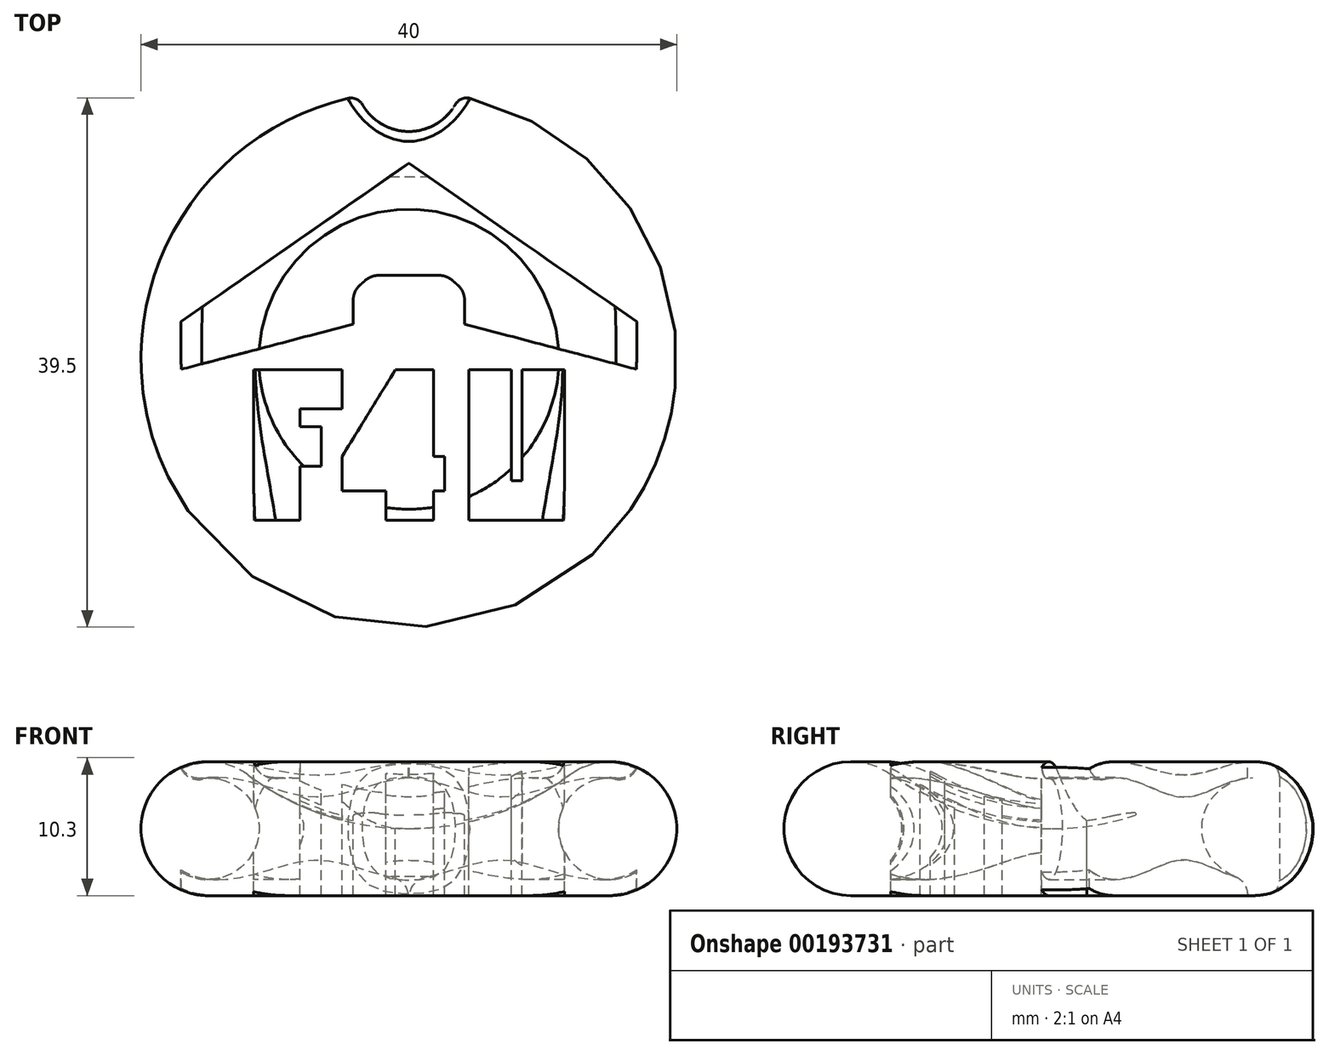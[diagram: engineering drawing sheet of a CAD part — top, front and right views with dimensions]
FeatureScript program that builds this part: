
annotation { "Feature Type Name" : "Feature", "Feature Type Description" : "" }
export const myFeature = defineFeature(function(context is Context, id is Id, definition is map)
    precondition{}
    {
        {
            var Q0;
            Q0=qCreatedBy(makeId("Front.planeOp"),FACE);
            var sketch = newSketch(context, id + "F0", { "sketchPlane" : qUnion([Q0])});
            skArc(sketch, "E0", {"start": v(-12, 9) * mm, "mid": v(-19.74, 6.58) * mm, "end": v(-15, 0) * mm});
            skArc(sketch, "E1", {"start": v(-12, 9) * mm, "mid": v(-6.32, 6.03) * mm, "end": v(0, 5) * mm});
            skLineSegment(sketch, "E2", {"start": v(-15, 0) * mm, "end": v(0, 0) * mm});
            skLineSegment(sketch, "E3", {"start": v(0, 0) * mm, "end": v(0, 5) * mm});
            skSolve(sketch);
        }
        {
            var Q0;
            Q0=makeQuery(id+"F0.imprint","IMPRINT",FACE,{"disambiguationData":[TD([[makeQuery(id+"F0.imprint","IMPRINT",EDGE,{"derivedFrom":sQuery(id+"F0.wireOp",EDGE,"E0")}),1.0]])]});
            var Q1;
            Q1=sQuery(id+"F0.wireOp",EDGE,"E3");
            revolve(context, id + "F1", {"entities" : qUnion([Q0]), "axis" : qUnion([Q1]), "revolveType" : RevolveType.FULL});
        }
        {
            var Q0;
            Q0=qCreatedBy(makeId("Top.planeOp"),FACE);
            cPlane(context, id + "F2", {"entities" : qUnion([Q0]), "cplaneType" : CPlaneType.OFFSET, "offset" : 10 * mm, "width" : 150 * mm, "height" : 150 * mm});
        }
        {
            var Q0;
            Q0=qCreatedBy(id+"F2.planeOp",FACE);
            var sketch = newSketch(context, id + "F3", { "sketchPlane" : qUnion([Q0])});
            skLineSegment(sketch, "E4", {"start": v(-11.6, -0.8) * mm, "end": v(-11.6, -12.04) * mm});
            skLineSegment(sketch, "E5", {"start": v(-11.6, -0.8) * mm, "end": v(-4.99, -0.8) * mm});
            skLineSegment(sketch, "E6", {"start": v(-4.99, -3.7) * mm, "end": v(-4.99, -0.8) * mm});
            skLineSegment(sketch, "E7", {"start": v(-6.55, -5.03) * mm, "end": v(-6.53, -8) * mm});
            skLineSegment(sketch, "E8", {"start": v(-4.99, -3.7) * mm, "end": v(-8.11, -3.7) * mm});
            skLineSegment(sketch, "E9", {"start": v(-6.55, -5.03) * mm, "end": v(-8.11, -5.03) * mm});
            skLineSegment(sketch, "E10", {"start": v(-6.53, -8) * mm, "end": v(-8.11, -8) * mm});
            skLineSegment(sketch, "E11", {"start": v(-11.6, -12.04) * mm, "end": v(-8.11, -12.04) * mm});
            skLineSegment(sketch, "E12", {"start": v(-8.11, -8) * mm, "end": v(-8.11, -12.04) * mm});
            skLineSegment(sketch, "E13", {"start": v(-8.11, -3.7) * mm, "end": v(-8.11, -5.03) * mm});
            skLineSegment(sketch, "E14", {"start": v(-1, -0.8) * mm, "end": v(1.86, -0.8) * mm});
            skLineSegment(sketch, "E15", {"start": v(-4.99, -7.27) * mm, "end": v(-1, -0.8) * mm});
            skLineSegment(sketch, "E16", {"start": v(1.86, -0.8) * mm, "end": v(1.86, -7.27) * mm});
            skLineSegment(sketch, "E17", {"start": v(-4.99, -7.27) * mm, "end": v(-4.99, -9.84) * mm});
            skLineSegment(sketch, "E18", {"start": v(1.86, -7.27) * mm, "end": v(2.66, -7.27) * mm});
            skLineSegment(sketch, "E19", {"start": v(-4.99, -9.84) * mm, "end": v(-1.7, -9.84) * mm});
            skLineSegment(sketch, "E20", {"start": v(2.66, -7.27) * mm, "end": v(2.66, -9.84) * mm});
            skLineSegment(sketch, "E21", {"start": v(-1.7, -9.84) * mm, "end": v(-1.7, -12.04) * mm});
            skLineSegment(sketch, "E22", {"start": v(2.66, -9.84) * mm, "end": v(1.86, -9.84) * mm});
            skLineSegment(sketch, "E23", {"start": v(-1.7, -12.04) * mm, "end": v(1.86, -12.04) * mm});
            skLineSegment(sketch, "E24", {"start": v(1.86, -9.84) * mm, "end": v(1.86, -12.04) * mm});
            skLineSegment(sketch, "E25", {"start": v(4.47, -0.8) * mm, "end": v(4.47, -12.04) * mm});
            skLineSegment(sketch, "E26", {"start": v(4.47, -0.8) * mm, "end": v(7.65, -0.8) * mm});
            skLineSegment(sketch, "E27", {"start": v(4.47, -12.04) * mm, "end": v(7.65, -12.04) * mm});
            skLineSegment(sketch, "E28", {"start": v(7.65, -0.8) * mm, "end": v(7.65, -9.08) * mm});
            skLineSegment(sketch, "E29", {"start": v(7.65, -9.08) * mm, "end": v(8.45, -9.08) * mm});
            skLineSegment(sketch, "E30", {"start": v(7.65, -12.04) * mm, "end": v(8.45, -12.04) * mm});
            skLineSegment(sketch, "E31", {"start": v(8.45, -9.08) * mm, "end": v(8.45, -0.8) * mm});
            skLineSegment(sketch, "E32", {"start": v(8.45, -12.04) * mm, "end": v(11.62, -12.04) * mm});
            skLineSegment(sketch, "E33", {"start": v(8.45, -0.8) * mm, "end": v(11.62, -0.8) * mm});
            skLineSegment(sketch, "E34", {"start": v(11.62, -12.04) * mm, "end": v(11.62, -0.8) * mm});
            skSolve(sketch);
        }
        {
            var Q0;
            Q0 = qSketchRegion(id + "F3", true);
            extrude(context, id + "F4", {"entities" : qUnion([Q0]), "operationType" : NewBodyOperationType.REMOVE, "oppositeDirection" : true, "depth" : 25 * mm});
        }
        {
            var Q0;
            Q0=qCreatedBy(makeId("Top.planeOp"),FACE);
            cPlane(context, id + "F5", {"entities" : qUnion([Q0]), "cplaneType" : CPlaneType.OFFSET, "offset" : 25 * mm, "width" : 150 * mm, "height" : 150 * mm});
        }
        {
            var Q0;
            Q0=qCreatedBy(id+"F5.planeOp",FACE);
            var sketch = newSketch(context, id + "F6", { "sketchPlane" : qUnion([Q0])});
            skLineSegment(sketch, "E35", {"start": v(-17, -0.76) * mm, "end": v(-4.16, 2.62) * mm});
            skLineSegment(sketch, "E36", {"start": v(-2.83, 6.25) * mm, "end": v(0, 6.26) * mm});
            skLineSegment(sketch, "E37", {"start": v(17, -0.76) * mm, "end": v(4.16, 2.62) * mm});
            skLineSegment(sketch, "E38", {"start": v(17.01, 2.8) * mm, "end": v(17, -0.76) * mm});
            skLineSegment(sketch, "E39", {"start": v(17.01, 2.8) * mm, "end": v(0.04, 14.6) * mm});
            skLineSegment(sketch, "E40", {"start": v(0.04, 14.6) * mm, "end": v(0.01, 14.6) * mm});
            skLineSegment(sketch, "E41", {"start": v(0.01, 14.6) * mm, "end": v(-0.01, 14.6) * mm});
            skLineSegment(sketch, "E42", {"start": v(-0.01, 14.6) * mm, "end": v(-0.04, 14.6) * mm});
            skLineSegment(sketch, "E43", {"start": v(-0.04, 14.6) * mm, "end": v(-17.01, 2.8) * mm});
            skLineSegment(sketch, "E44", {"start": v(-17.01, 2.8) * mm, "end": v(-17, -0.76) * mm});
            skLineSegment(sketch, "E45", {"start": v(2.83, 6.25) * mm, "end": v(0, 6.26) * mm});
            skLineSegment(sketch, "E46", {"start": v(-4.16, 2.62) * mm, "end": v(-4.16, 5.08) * mm});
            skLineSegment(sketch, "E47", {"start": v(-2.83, 6.25) * mm, "end": v(-4.16, 5.08) * mm});
            skLineSegment(sketch, "E48", {"start": v(4.16, 2.62) * mm, "end": v(4.16, 5.08) * mm});
            skLineSegment(sketch, "E49", {"start": v(2.83, 6.25) * mm, "end": v(4.16, 5.08) * mm});
            skSolve(sketch);
        }
        {
            var Q0;
            Q0 = qSketchRegion(id + "F6", true);
            extrude(context, id + "F7", {"entities" : qUnion([Q0]), "operationType" : NewBodyOperationType.REMOVE, "oppositeDirection" : true, "depth" : 45 * mm});
        }
        {
            var Q0;
            Q0=qCreatedBy(makeId("Front.planeOp"),FACE);
            var sketch = newSketch(context, id + "F8", { "sketchPlane" : qUnion([Q0])});
            skCircle(sketch, "E50", {"center": v(-15, 5) * mm, "radius": 3.8 * mm});
            skSolve(sketch);
        }
        {
            var Q0;
            Q0 = qSketchRegion(id + "F8", true);
            var Q1;
            Q1=sQuery(id+"F0.wireOp",EDGE,"E3");
            revolve(context, id + "F9", {"operationType" : NewBodyOperationType.ADD, "entities" : qUnion([Q0]), "axis" : qUnion([Q1]), "revolveType" : RevolveType.FULL});
        }
        {
            var Q0;
            Q0=qCreatedBy(makeId("Top.planeOp"),FACE);
            var sketch = newSketch(context, id + "F10", { "sketchPlane" : qUnion([Q0])});
            skCircle(sketch, "E51", {"center": v(0, 21) * mm, "radius": 4 * mm});
            skSolve(sketch);
        }
        {
            var Q0;
            Q0 = qSketchRegion(id + "F10", true);
            extrude(context, id + "F11", {"entities" : qUnion([Q0]), "operationType" : NewBodyOperationType.REMOVE, "depth" : 25 * mm});
        }
        {
            var Q0;
            Q0=makeQuery(id+"F11.boolean.opBoolean","INTERSECT",EDGE,{"derivedFrom":[makeQuery(id+"F4.boolean.opBoolean","SPLIT",FACE,{"disambiguationData":[TD([makeQuery(id+"F1.opRevolve","SWEPT_FACE",FACE,{"disambiguationData":[OSD([sQuery(id+"F0.wireOp",EDGE,"E2")])]})])],"derivedFrom":makeQuery(id+"F1.opRevolve","SWEPT_FACE",FACE,{"disambiguationData":[OSD([sQuery(id+"F0.wireOp",EDGE,"E0")])]})}),makeQuery(id+"F11.opExtrude","SWEPT_FACE",FACE,{"disambiguationData":[OSD([sQuery(id+"F10.wireOp",EDGE,"E51")])]})]});
            fillet(context, id + "F12", {"entities" : qUnion([Q0]), "radius" : 1 * mm, "tangentPropagation" : true, "allowEdgeOverflow" : false});
        }
        {
            var Q0;
            Q0=makeQuery(id+"F9.boolean.opBoolean","INTERSECT",EDGE,{"disambiguationData":[OD(0.0)],"derivedFrom":[makeQuery(id+"F4.boolean.opBoolean","COPY",FACE,{"derivedFrom":makeQuery(id+"F4.opExtrude","SWEPT_FACE",FACE,{"disambiguationData":[OSD([sQuery(id+"F3.wireOp",EDGE,"E4")])]})}),makeQuery(id+"F9.opRevolve","SWEPT_FACE",FACE,{"disambiguationData":[OSD([sQuery(id+"F8.wireOp",EDGE,"E50")])]})]});
            var Q1;
            Q1=makeQuery(id+"F9.boolean.opBoolean","INTERSECT",EDGE,{"disambiguationData":[OD(0.0)],"derivedFrom":[makeQuery(id+"F4.boolean.opBoolean","COPY",FACE,{"derivedFrom":makeQuery(id+"F4.opExtrude","SWEPT_FACE",FACE,{"disambiguationData":[OSD([sQuery(id+"F3.wireOp",EDGE,"E34")])]})}),makeQuery(id+"F9.opRevolve","SWEPT_FACE",FACE,{"disambiguationData":[OSD([sQuery(id+"F8.wireOp",EDGE,"E50")])]})]});
            var Q2;
            Q2=makeQuery(id+"F9.boolean.opBoolean","INTERSECT",EDGE,{"disambiguationData":[OD(0.0)],"derivedFrom":[makeQuery(id+"F7.boolean.opBoolean","COPY",FACE,{"derivedFrom":makeQuery(id+"F7.opExtrude","SWEPT_FACE",FACE,{"disambiguationData":[OSD([sQuery(id+"F6.wireOp",EDGE,"E38")])]})}),makeQuery(id+"F9.opRevolve","SWEPT_FACE",FACE,{"disambiguationData":[OSD([sQuery(id+"F8.wireOp",EDGE,"E50")])]})]});
            var Q3;
            Q3=makeQuery(id+"F9.boolean.opBoolean","INTERSECT",EDGE,{"disambiguationData":[OD(0.0)],"derivedFrom":[makeQuery(id+"F7.boolean.opBoolean","COPY",FACE,{"derivedFrom":makeQuery(id+"F7.opExtrude","SWEPT_FACE",FACE,{"disambiguationData":[OSD([sQuery(id+"F6.wireOp",EDGE,"E40"),sQuery(id+"F6.wireOp",EDGE,"E41"),sQuery(id+"F6.wireOp",EDGE,"E42")])]})}),makeQuery(id+"F9.opRevolve","SWEPT_FACE",FACE,{"disambiguationData":[OSD([sQuery(id+"F8.wireOp",EDGE,"E50")])]})]});
            var Q4;
            Q4=makeQuery(id+"F9.boolean.opBoolean","INTERSECT",EDGE,{"disambiguationData":[OD(0.0)],"derivedFrom":[makeQuery(id+"F7.boolean.opBoolean","COPY",FACE,{"derivedFrom":makeQuery(id+"F7.opExtrude","SWEPT_FACE",FACE,{"disambiguationData":[OSD([sQuery(id+"F6.wireOp",EDGE,"E44")])]})}),makeQuery(id+"F9.opRevolve","SWEPT_FACE",FACE,{"disambiguationData":[OSD([sQuery(id+"F8.wireOp",EDGE,"E50")])]})]});
            var Q5;
            Q5=makeQuery(id+"F9.boolean.opBoolean","INTERSECT",EDGE,{"disambiguationData":[OD(0.0)],"derivedFrom":[makeQuery(id+"F4.boolean.opBoolean","COPY",FACE,{"derivedFrom":makeQuery(id+"F4.opExtrude","SWEPT_FACE",FACE,{"disambiguationData":[OSD([sQuery(id+"F3.wireOp",EDGE,"E4")])]})}),makeQuery(id+"F9.opRevolve","SWEPT_FACE",FACE,{"disambiguationData":[OSD([sQuery(id+"F8.wireOp",EDGE,"E50")])]})]});
            var Q6;
            Q6=makeQuery(id+"F9.boolean.opBoolean","INTERSECT",EDGE,{"disambiguationData":[OD(0.0)],"derivedFrom":[makeQuery(id+"F4.boolean.opBoolean","COPY",FACE,{"derivedFrom":makeQuery(id+"F4.opExtrude","SWEPT_FACE",FACE,{"disambiguationData":[OSD([sQuery(id+"F3.wireOp",EDGE,"E34")])]})}),makeQuery(id+"F9.opRevolve","SWEPT_FACE",FACE,{"disambiguationData":[OSD([sQuery(id+"F8.wireOp",EDGE,"E50")])]})]});
            var Q7;
            Q7=makeQuery(id+"F9.boolean.opBoolean","INTERSECT",EDGE,{"disambiguationData":[OD(0.0)],"derivedFrom":[makeQuery(id+"F7.boolean.opBoolean","COPY",FACE,{"derivedFrom":makeQuery(id+"F7.opExtrude","SWEPT_FACE",FACE,{"disambiguationData":[OSD([sQuery(id+"F6.wireOp",EDGE,"E38")])]})}),makeQuery(id+"F9.opRevolve","SWEPT_FACE",FACE,{"disambiguationData":[OSD([sQuery(id+"F8.wireOp",EDGE,"E50")])]})]});
            var Q8;
            Q8=makeQuery(id+"F9.boolean.opBoolean","INTERSECT",EDGE,{"disambiguationData":[OD(0.0)],"derivedFrom":[makeQuery(id+"F7.boolean.opBoolean","COPY",FACE,{"derivedFrom":makeQuery(id+"F7.opExtrude","SWEPT_FACE",FACE,{"disambiguationData":[OSD([sQuery(id+"F6.wireOp",EDGE,"E40"),sQuery(id+"F6.wireOp",EDGE,"E41"),sQuery(id+"F6.wireOp",EDGE,"E42")])]})}),makeQuery(id+"F9.opRevolve","SWEPT_FACE",FACE,{"disambiguationData":[OSD([sQuery(id+"F8.wireOp",EDGE,"E50")])]})]});
            var Q9;
            Q9=makeQuery(id+"F9.boolean.opBoolean","INTERSECT",EDGE,{"disambiguationData":[OD(0.0)],"derivedFrom":[makeQuery(id+"F7.boolean.opBoolean","COPY",FACE,{"derivedFrom":makeQuery(id+"F7.opExtrude","SWEPT_FACE",FACE,{"disambiguationData":[OSD([sQuery(id+"F6.wireOp",EDGE,"E44")])]})}),makeQuery(id+"F9.opRevolve","SWEPT_FACE",FACE,{"disambiguationData":[OSD([sQuery(id+"F8.wireOp",EDGE,"E50")])]})]});
            var Q10;
            Q10=makeQuery(id+"F7.boolean.opBoolean","COPY",EDGE,{"derivedFrom":makeQuery(id+"F7.opExtrude","SWEPT_EDGE",EDGE,{"disambiguationData":[OSD([sQuery(id+"F6.wireOp",EDGE,"E48"),sQuery(id+"F6.wireOp",EDGE,"E49")])]})});
            var Q11;
            Q11=makeQuery(id+"F7.boolean.opBoolean","COPY",EDGE,{"derivedFrom":makeQuery(id+"F7.opExtrude","SWEPT_EDGE",EDGE,{"disambiguationData":[OSD([sQuery(id+"F6.wireOp",EDGE,"E45"),sQuery(id+"F6.wireOp",EDGE,"E49")])]})});
            var Q12;
            Q12=makeQuery(id+"F7.boolean.opBoolean","COPY",EDGE,{"derivedFrom":makeQuery(id+"F7.opExtrude","SWEPT_EDGE",EDGE,{"disambiguationData":[OSD([sQuery(id+"F6.wireOp",EDGE,"E36"),sQuery(id+"F6.wireOp",EDGE,"E47")])]})});
            var Q13;
            Q13=makeQuery(id+"F7.boolean.opBoolean","COPY",EDGE,{"derivedFrom":makeQuery(id+"F7.opExtrude","SWEPT_EDGE",EDGE,{"disambiguationData":[OSD([sQuery(id+"F6.wireOp",EDGE,"E46"),sQuery(id+"F6.wireOp",EDGE,"E47")])]})});
            var Q14;
            Q14=makeQuery(id+"F9.boolean.opBoolean","INTERSECT",EDGE,{"disambiguationData":[OD(0.0)],"derivedFrom":[makeQuery(id+"F4.boolean.opBoolean","COPY",FACE,{"derivedFrom":makeQuery(id+"F4.opExtrude","SWEPT_FACE",FACE,{"disambiguationData":[OSD([sQuery(id+"F3.wireOp",EDGE,"E4")])]})}),makeQuery(id+"F9.opRevolve","SWEPT_FACE",FACE,{"disambiguationData":[OSD([sQuery(id+"F8.wireOp",EDGE,"E50")])]})]});
            var Q15;
            Q15=makeQuery(id+"F9.boolean.opBoolean","INTERSECT",EDGE,{"disambiguationData":[OD(0.0)],"derivedFrom":[makeQuery(id+"F4.boolean.opBoolean","COPY",FACE,{"derivedFrom":makeQuery(id+"F4.opExtrude","SWEPT_FACE",FACE,{"disambiguationData":[OSD([sQuery(id+"F3.wireOp",EDGE,"E34")])]})}),makeQuery(id+"F9.opRevolve","SWEPT_FACE",FACE,{"disambiguationData":[OSD([sQuery(id+"F8.wireOp",EDGE,"E50")])]})]});
            var Q16;
            Q16=makeQuery(id+"F9.boolean.opBoolean","INTERSECT",EDGE,{"disambiguationData":[OD(0.0)],"derivedFrom":[makeQuery(id+"F7.boolean.opBoolean","COPY",FACE,{"derivedFrom":makeQuery(id+"F7.opExtrude","SWEPT_FACE",FACE,{"disambiguationData":[OSD([sQuery(id+"F6.wireOp",EDGE,"E38")])]})}),makeQuery(id+"F9.opRevolve","SWEPT_FACE",FACE,{"disambiguationData":[OSD([sQuery(id+"F8.wireOp",EDGE,"E50")])]})]});
            var Q17;
            Q17=makeQuery(id+"F9.boolean.opBoolean","INTERSECT",EDGE,{"disambiguationData":[OD(0.0)],"derivedFrom":[makeQuery(id+"F7.boolean.opBoolean","COPY",FACE,{"derivedFrom":makeQuery(id+"F7.opExtrude","SWEPT_FACE",FACE,{"disambiguationData":[OSD([sQuery(id+"F6.wireOp",EDGE,"E40"),sQuery(id+"F6.wireOp",EDGE,"E41"),sQuery(id+"F6.wireOp",EDGE,"E42")])]})}),makeQuery(id+"F9.opRevolve","SWEPT_FACE",FACE,{"disambiguationData":[OSD([sQuery(id+"F8.wireOp",EDGE,"E50")])]})]});
            var Q18;
            Q18=makeQuery(id+"F9.boolean.opBoolean","INTERSECT",EDGE,{"disambiguationData":[OD(0.0)],"derivedFrom":[makeQuery(id+"F7.boolean.opBoolean","COPY",FACE,{"derivedFrom":makeQuery(id+"F7.opExtrude","SWEPT_FACE",FACE,{"disambiguationData":[OSD([sQuery(id+"F6.wireOp",EDGE,"E44")])]})}),makeQuery(id+"F9.opRevolve","SWEPT_FACE",FACE,{"disambiguationData":[OSD([sQuery(id+"F8.wireOp",EDGE,"E50")])]})]});
            fillet(context, id + "F13", {"entities" : qUnion([Q0, Q1, Q2, Q3, Q4, Q5, Q6, Q7, Q8, Q9, Q10, Q11, Q12, Q13, Q14, Q15, Q16, Q17, Q18]), "radius" : 1.5 * mm, "tangentPropagation" : true, "allowEdgeOverflow" : false});
        }
    });
